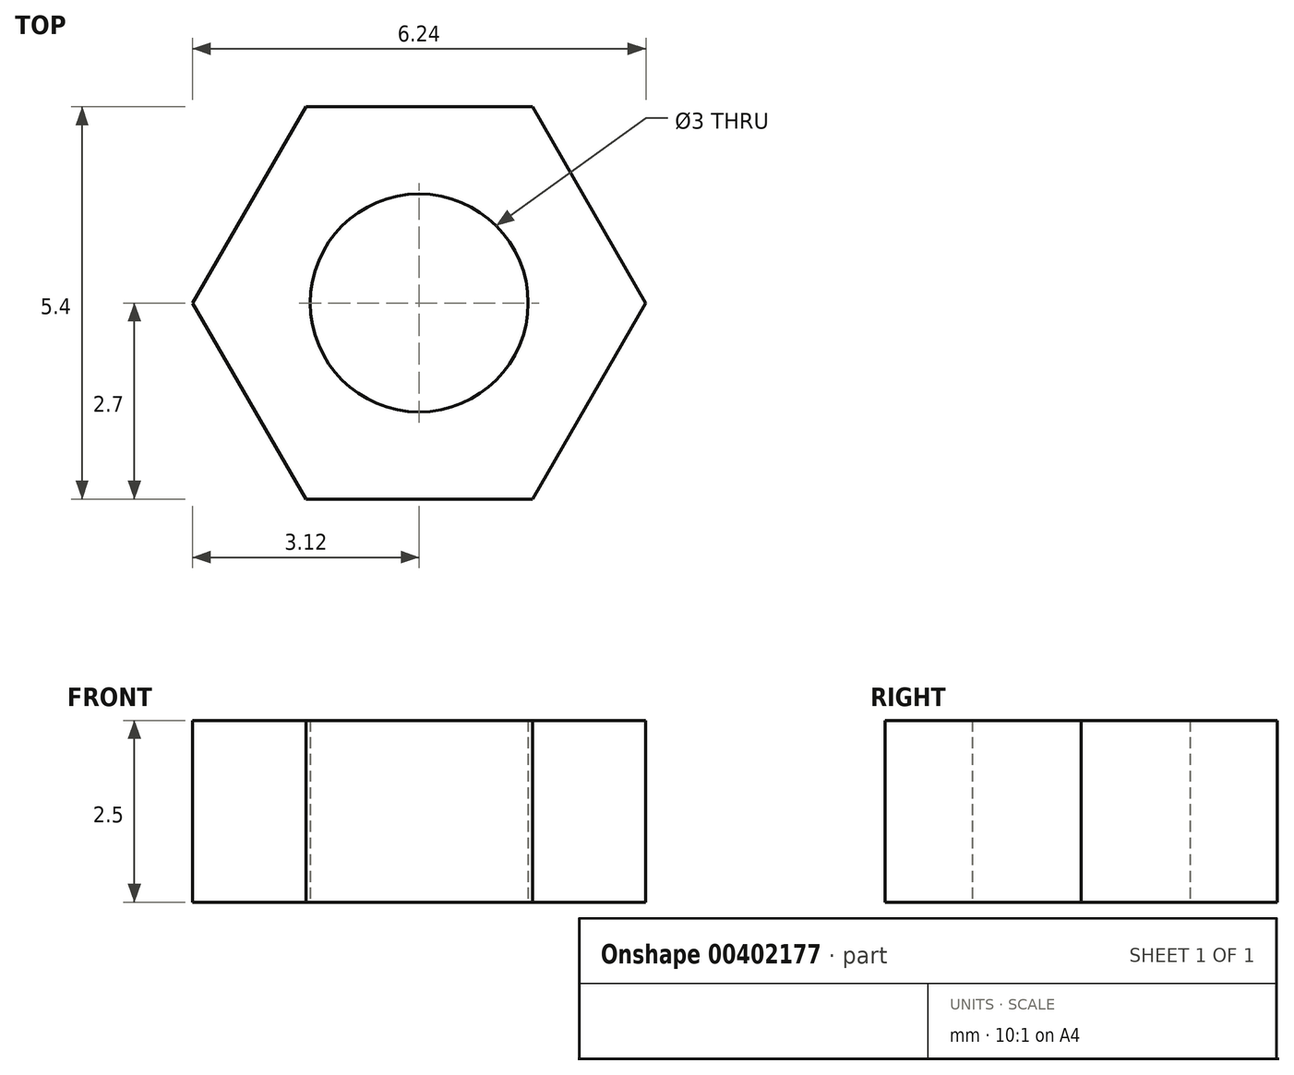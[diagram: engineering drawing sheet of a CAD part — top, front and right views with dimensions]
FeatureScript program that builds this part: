
annotation { "Feature Type Name" : "Feature", "Feature Type Description" : "" }
export const myFeature = defineFeature(function(context is Context, id is Id, definition is map)
    precondition{}
    {
        {
            var Q0;
            Q0=qCreatedBy(makeId("Top.planeOp"),FACE);
            var sketch = newSketch(context, id + "F0", { "sketchPlane" : qUnion([Q0])});
            skPoint(sketch, "E0.middle", {"position": v(0, 0) * mm});
            skCircle(sketch, "E1.cCircle", {"center": v(0, 0) * mm, "radius": 2.7 * mm, "construction": true});
            skLineSegment(sketch, "E1.0", {"start": v(-1.56, 2.7) * mm, "end": v(1.56, 2.7) * mm});
            skLineSegment(sketch, "E1.1", {"start": v(1.56, 2.7) * mm, "end": v(3.12, 0) * mm});
            skLineSegment(sketch, "E1.2", {"start": v(3.12, 0) * mm, "end": v(1.56, -2.7) * mm});
            skLineSegment(sketch, "E1.3", {"start": v(1.56, -2.7) * mm, "end": v(-1.56, -2.7) * mm});
            skLineSegment(sketch, "E1.4", {"start": v(-1.56, -2.7) * mm, "end": v(-3.12, 0) * mm});
            skLineSegment(sketch, "E1.5", {"start": v(-3.12, 0) * mm, "end": v(-1.56, 2.7) * mm});
            skPoint(sketch, "E1.0.midPoint", {"position": v(0, 2.7) * mm});
            skCircle(sketch, "E2", {"center": v(0, 0) * mm, "radius": 1.5 * mm});
            skSolve(sketch);
        }
        {
            var Q0;
            Q0=qSketchRegion(id+"F0",true);
            extrude(context, id + "F1", {"entities" : qUnion([Q0]), "depth" : 2.5 * mm});
        }
    });
